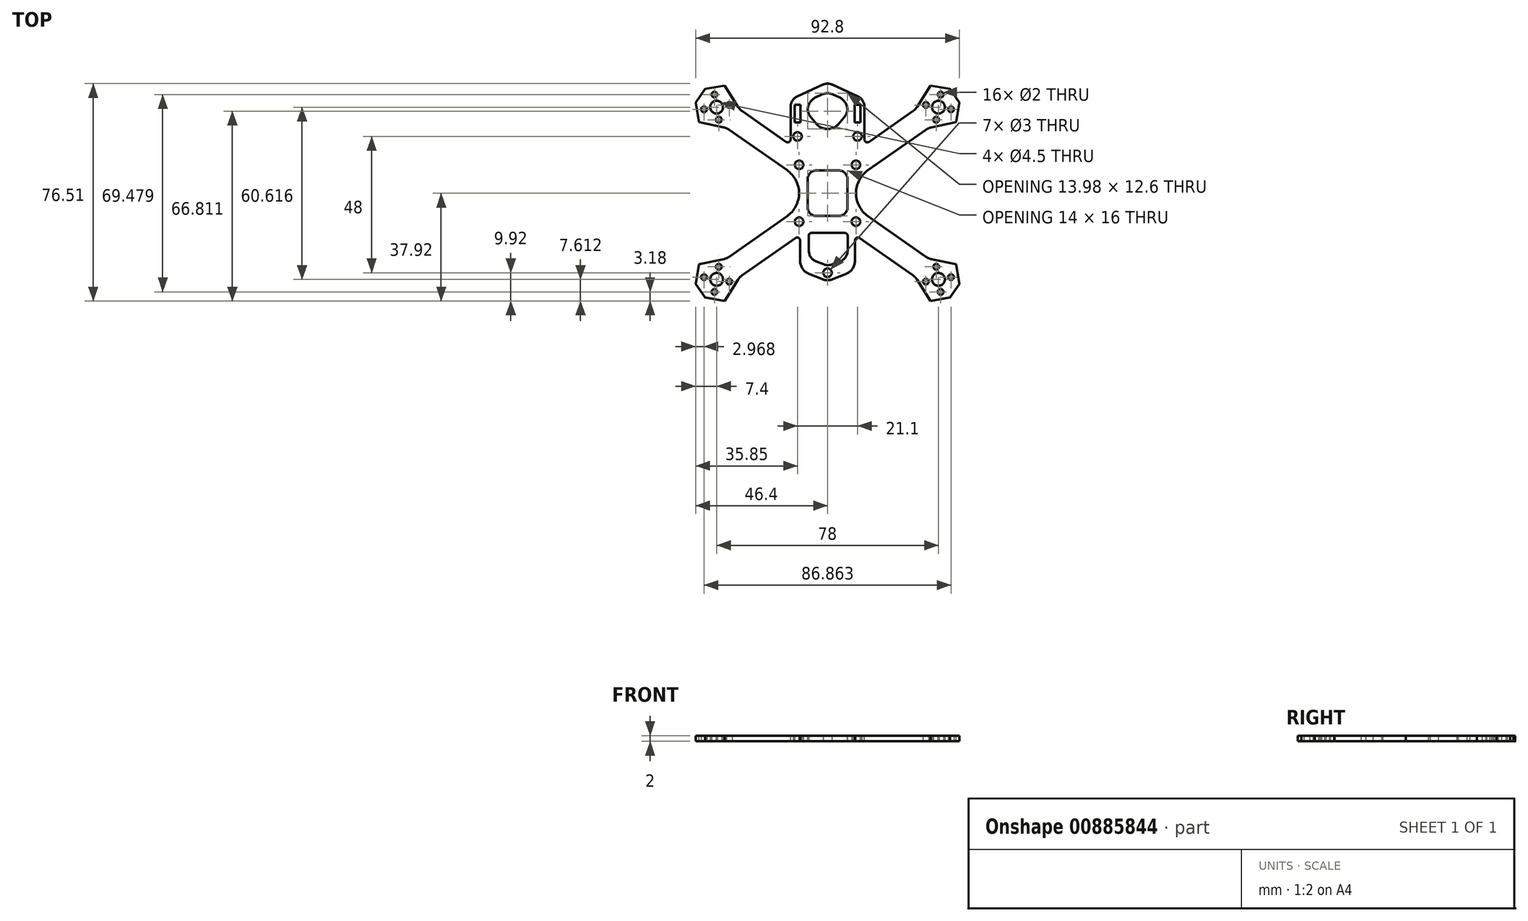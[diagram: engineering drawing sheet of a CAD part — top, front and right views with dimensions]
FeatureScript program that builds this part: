
annotation { "Feature Type Name" : "Feature", "Feature Type Description" : "" }
export const myFeature = defineFeature(function(context is Context, id is Id, definition is map)
    precondition{}
    {
        {
            var Q0;
            Q0=qCreatedBy(makeId("Top.planeOp"),FACE);
            var sketch = newSketch(context, id + "F0", { "sketchPlane" : qUnion([Q0])});
            skLineSegment(sketch, "E0.bottom", {"start": v(10, 10) * mm, "end": v(-10, 10) * mm, "construction": true});
            skLineSegment(sketch, "E0.top", {"start": v(10, -10) * mm, "end": v(-10, -10) * mm, "construction": true});
            skLineSegment(sketch, "E0.left", {"start": v(10, 10) * mm, "end": v(10, -10) * mm, "construction": true});
            skLineSegment(sketch, "E0.right", {"start": v(-10, 10) * mm, "end": v(-10, -10) * mm, "construction": true});
            skPoint(sketch, "E0.middle", {"position": v(0, 0) * mm});
            skCircle(sketch, "E1", {"center": v(-10, 10) * mm, "radius": 1.5 * mm});
            skCircle(sketch, "E2", {"center": v(10, 10) * mm, "radius": 1.5 * mm});
            skCircle(sketch, "E3", {"center": v(10, -10) * mm, "radius": 1.5 * mm});
            skCircle(sketch, "E4", {"center": v(-10, -10) * mm, "radius": 1.5 * mm});
            skLineSegment(sketch, "E5.bottom", {"start": v(13, 13) * mm, "end": v(-13, 13) * mm});
            skLineSegment(sketch, "E5.top", {"start": v(13, -13) * mm, "end": v(-13, -13) * mm});
            skLineSegment(sketch, "E5.left", {"start": v(13, 13) * mm, "end": v(13, -13) * mm});
            skLineSegment(sketch, "E5.right", {"start": v(-13, 13) * mm, "end": v(-13, -13) * mm});
            skLineSegment(sketch, "E6.bottom", {"start": v(-13, 13) * mm, "end": v(13, 13) * mm});
            skLineSegment(sketch, "E6.top", {"start": v(-13, 33) * mm, "end": v(13, 33) * mm});
            skLineSegment(sketch, "E6.left", {"start": v(-13, 13) * mm, "end": v(-13, 33) * mm});
            skLineSegment(sketch, "E6.right", {"start": v(13, 13) * mm, "end": v(13, 33) * mm});
            skLineSegment(sketch, "E7.bottom", {"start": v(-11.6, 24.9) * mm, "end": v(-9.5, 24.9) * mm});
            skLineSegment(sketch, "E7.top", {"start": v(-11.6, 31.1) * mm, "end": v(-9.5, 31.1) * mm});
            skLineSegment(sketch, "E7.left", {"start": v(-11.6, 24.9) * mm, "end": v(-11.6, 31.1) * mm});
            skLineSegment(sketch, "E7.right", {"start": v(-9.5, 24.9) * mm, "end": v(-9.5, 31.1) * mm});
            skLineSegment(sketch, "E8.bottom", {"start": v(9.5, 24.9) * mm, "end": v(11.6, 24.9) * mm});
            skLineSegment(sketch, "E8.top", {"start": v(9.5, 31.1) * mm, "end": v(11.6, 31.1) * mm});
            skLineSegment(sketch, "E8.left", {"start": v(9.5, 24.9) * mm, "end": v(9.5, 31.1) * mm});
            skLineSegment(sketch, "E8.right", {"start": v(11.6, 24.9) * mm, "end": v(11.6, 31.1) * mm});
            skLineSegment(sketch, "E9.bottom", {"start": v(-13, -13) * mm, "end": v(13, -13) * mm});
            skLineSegment(sketch, "E9.top", {"start": v(-13, -31) * mm, "end": v(13, -31) * mm});
            skLineSegment(sketch, "E9.left", {"start": v(-13, -13) * mm, "end": v(-13, -31) * mm});
            skLineSegment(sketch, "E9.right", {"start": v(13, -13) * mm, "end": v(13, -31) * mm});
            skCircle(sketch, "E10", {"center": v(-39, 30.3) * mm, "radius": 25.5 * mm, "construction": true});
            skCircle(sketch, "E11", {"center": v(39, 30.3) * mm, "radius": 25.5 * mm, "construction": true});
            skLineSegment(sketch, "E12", {"start": v(0, 0) * mm, "end": v(0, 3) * mm, "construction": true});
            skLineSegment(sketch, "E13", {"start": v(0, 3) * mm, "end": v(65.53, 48.89) * mm, "construction": true});
            skLineSegment(sketch, "E14", {"start": v(0, 3) * mm, "end": v(-65.53, 48.89) * mm, "construction": true});
            skCircle(sketch, "E15", {"center": v(-10.55, 20) * mm, "radius": 1.5 * mm});
            skPoint(sketch, "E15.centerSnap0", {"position": v(-10.55, 31.1) * mm});
            skCircle(sketch, "E16", {"center": v(10.55, 20) * mm, "radius": 1.5 * mm});
            skPoint(sketch, "E16.centerSnap0", {"position": v(10.55, 31.1) * mm});
            skLineSegment(sketch, "E17", {"start": v(34.98, 36.04) * mm, "end": v(43.02, 24.57) * mm, "construction": true});
            skArc(sketch, "E18", {"start": v(34.98, 36.04) * mm, "mid": v(44.73, 34.32) * mm, "end": v(43.02, 24.57) * mm});
            skLineSegment(sketch, "E19", {"start": v(34.98, 36.04) * mm, "end": v(13, 20.65) * mm});
            skLineSegment(sketch, "E20", {"start": v(43.02, 24.57) * mm, "end": v(13, 3.56) * mm});
            skLineSegment(sketch, "E21", {"start": v(-34.98, 36.04) * mm, "end": v(-43.02, 24.57) * mm, "construction": true});
            skArc(sketch, "E22", {"start": v(-43.02, 24.57) * mm, "mid": v(-44.73, 34.32) * mm, "end": v(-34.98, 36.04) * mm});
            skLineSegment(sketch, "E23", {"start": v(-34.98, 36.04) * mm, "end": v(-13, 20.65) * mm});
            skLineSegment(sketch, "E24", {"start": v(-43.02, 24.57) * mm, "end": v(-13, 3.56) * mm});
            skCircle(sketch, "E25", {"center": v(-39, 30.3) * mm, "radius": 4.5 * mm, "construction": true});
            skCircle(sketch, "E26", {"center": v(-43.43, 29.53) * mm, "radius": 1 * mm});
            skCircle(sketch, "E27", {"center": v(-34.57, 31.09) * mm, "radius": 1 * mm});
            skCircle(sketch, "E28", {"center": v(-39.78, 34.74) * mm, "radius": 1 * mm});
            skCircle(sketch, "E29", {"center": v(-38.22, 25.88) * mm, "radius": 1 * mm});
            skCircle(sketch, "E30", {"center": v(-39, 30.3) * mm, "radius": 2.25 * mm});
            skLineSegment(sketch, "E31", {"start": v(0, 0) * mm, "end": v(0, -3) * mm, "construction": true});
            skLineSegment(sketch, "E32", {"start": v(0, -3) * mm, "end": v(65.53, -48.89) * mm, "construction": true});
            skLineSegment(sketch, "E33", {"start": v(0, -3) * mm, "end": v(-65.53, -48.89) * mm, "construction": true});
            skLineSegment(sketch, "E34", {"start": v(34.98, -36.04) * mm, "end": v(43.02, -24.57) * mm, "construction": true});
            skCircle(sketch, "E35", {"center": v(39, -30.3) * mm, "radius": 25.5 * mm, "construction": true});
            skArc(sketch, "E36", {"start": v(43.02, -24.57) * mm, "mid": v(44.73, -34.32) * mm, "end": v(34.98, -36.04) * mm});
            skLineSegment(sketch, "E37", {"start": v(34.98, -36.04) * mm, "end": v(13, -20.65) * mm});
            skLineSegment(sketch, "E38", {"start": v(43.02, -24.57) * mm, "end": v(13, -3.56) * mm});
            skLineSegment(sketch, "E39", {"start": v(-43.02, -24.57) * mm, "end": v(-34.98, -36.04) * mm, "construction": true});
            skArc(sketch, "E40", {"start": v(-34.98, -36.04) * mm, "mid": v(-44.73, -34.32) * mm, "end": v(-43.02, -24.57) * mm});
            skLineSegment(sketch, "E41", {"start": v(-43.02, -24.57) * mm, "end": v(-13, -3.56) * mm});
            skLineSegment(sketch, "E42", {"start": v(-34.98, -36.04) * mm, "end": v(-13, -20.65) * mm});
            skCircle(sketch, "E43", {"center": v(39, 30.3) * mm, "radius": 4.5 * mm, "construction": true});
            skCircle(sketch, "E44", {"center": v(43.43, 29.53) * mm, "radius": 1 * mm});
            skCircle(sketch, "E45", {"center": v(34.57, 31.09) * mm, "radius": 1 * mm});
            skCircle(sketch, "E46", {"center": v(39.78, 34.74) * mm, "radius": 1 * mm});
            skCircle(sketch, "E47", {"center": v(38.22, 25.88) * mm, "radius": 1 * mm});
            skCircle(sketch, "E48", {"center": v(39, 30.3) * mm, "radius": 2.25 * mm});
            skCircle(sketch, "E49", {"center": v(-39, -30.3) * mm, "radius": 4.5 * mm, "construction": true});
            skCircle(sketch, "E50", {"center": v(-43.43, -29.53) * mm, "radius": 1 * mm});
            skCircle(sketch, "E51", {"center": v(-34.57, -31.09) * mm, "radius": 1 * mm});
            skCircle(sketch, "E52", {"center": v(-38.22, -25.88) * mm, "radius": 1 * mm});
            skCircle(sketch, "E53", {"center": v(-39.78, -34.74) * mm, "radius": 1 * mm});
            skCircle(sketch, "E54", {"center": v(-39, -30.3) * mm, "radius": 2.25 * mm});
            skCircle(sketch, "E55", {"center": v(39, -30.3) * mm, "radius": 4.5 * mm, "construction": true});
            skCircle(sketch, "E56", {"center": v(43.43, -29.53) * mm, "radius": 1 * mm});
            skCircle(sketch, "E57", {"center": v(38.22, -25.88) * mm, "radius": 1 * mm});
            skCircle(sketch, "E58", {"center": v(34.57, -31.09) * mm, "radius": 1 * mm});
            skCircle(sketch, "E59", {"center": v(39.78, -34.74) * mm, "radius": 1 * mm});
            skCircle(sketch, "E60", {"center": v(39, -30.3) * mm, "radius": 2.25 * mm});
            skCircle(sketch, "E61", {"center": v(-39, -30.3) * mm, "radius": 25.5 * mm, "construction": true});
            skCircle(sketch, "E62", {"center": v(0, -28) * mm, "radius": 1.5 * mm});
            skPoint(sketch, "E62.centerSnap0", {"position": v(0, -31) * mm});
            skLineSegment(sketch, "E63", {"start": v(-45.9, 29.1) * mm, "end": v(-32.1, 31.52) * mm, "construction": true});
            skLineSegment(sketch, "E64", {"start": v(-40.22, 37.2) * mm, "end": v(-37.78, 23.41) * mm, "construction": true});
            skLineSegment(sketch, "E65", {"start": v(40.22, 37.2) * mm, "end": v(37.78, 23.41) * mm, "construction": true});
            skLineSegment(sketch, "E66", {"start": v(45.9, 29.1) * mm, "end": v(32.1, 31.52) * mm, "construction": true});
            skLineSegment(sketch, "E67", {"start": v(-45.9, -29.1) * mm, "end": v(-32.1, -31.52) * mm, "construction": true});
            skLineSegment(sketch, "E68", {"start": v(-40.22, -37.2) * mm, "end": v(-37.78, -23.41) * mm, "construction": true});
            skLineSegment(sketch, "E69", {"start": v(45.9, -29.1) * mm, "end": v(32.1, -31.52) * mm, "construction": true});
            skLineSegment(sketch, "E70", {"start": v(40.22, -37.2) * mm, "end": v(37.78, -23.41) * mm, "construction": true});
            skSolve(sketch);
        }
        {
            var Q0;
            Q0 = qSketchRegion(id + "F0", true);
            extrude(context, id + "F1", {"entities" : qUnion([Q0]), "depth" : 2 * mm, "offsetDistance" : 25 * mm});
        }
        {
            var Q0;
            Q0=makeQuery(id+"F1.opExtrude","CAP_FACE",FACE,{"disambiguationData":[OSD([sQuery(id+"F0.wireOp",EDGE,"E1"),sQuery(id+"F0.wireOp",EDGE,"E2"),sQuery(id+"F0.wireOp",EDGE,"E3"),sQuery(id+"F0.wireOp",EDGE,"E4"),sQuery(id+"F0.wireOp",EDGE,"E5.left"),sQuery(id+"F0.wireOp",EDGE,"E5.right"),sQuery(id+"F0.wireOp",EDGE,"E6.top"),sQuery(id+"F0.wireOp",EDGE,"E6.left"),sQuery(id+"F0.wireOp",EDGE,"E6.right"),sQuery(id+"F0.wireOp",EDGE,"E7.bottom"),sQuery(id+"F0.wireOp",EDGE,"E7.top"),sQuery(id+"F0.wireOp",EDGE,"E7.left"),sQuery(id+"F0.wireOp",EDGE,"E7.right"),sQuery(id+"F0.wireOp",EDGE,"E8.bottom"),sQuery(id+"F0.wireOp",EDGE,"E8.top"),sQuery(id+"F0.wireOp",EDGE,"E8.left"),sQuery(id+"F0.wireOp",EDGE,"E8.right"),sQuery(id+"F0.wireOp",EDGE,"E9.top"),sQuery(id+"F0.wireOp",EDGE,"E9.left"),sQuery(id+"F0.wireOp",EDGE,"E9.right"),sQuery(id+"F0.wireOp",EDGE,"E15"),sQuery(id+"F0.wireOp",EDGE,"E16"),sQuery(id+"F0.wireOp",EDGE,"E18"),sQuery(id+"F0.wireOp",EDGE,"E19"),sQuery(id+"F0.wireOp",EDGE,"E20"),sQuery(id+"F0.wireOp",EDGE,"E22"),sQuery(id+"F0.wireOp",EDGE,"E23"),sQuery(id+"F0.wireOp",EDGE,"E24"),sQuery(id+"F0.wireOp",EDGE,"E26"),sQuery(id+"F0.wireOp",EDGE,"E27"),sQuery(id+"F0.wireOp",EDGE,"E28"),sQuery(id+"F0.wireOp",EDGE,"E29"),sQuery(id+"F0.wireOp",EDGE,"E30"),sQuery(id+"F0.wireOp",EDGE,"E36"),sQuery(id+"F0.wireOp",EDGE,"E37"),sQuery(id+"F0.wireOp",EDGE,"E38"),sQuery(id+"F0.wireOp",EDGE,"E40"),sQuery(id+"F0.wireOp",EDGE,"E41"),sQuery(id+"F0.wireOp",EDGE,"E42"),sQuery(id+"F0.wireOp",EDGE,"E44"),sQuery(id+"F0.wireOp",EDGE,"E45"),sQuery(id+"F0.wireOp",EDGE,"E46"),sQuery(id+"F0.wireOp",EDGE,"E47"),sQuery(id+"F0.wireOp",EDGE,"E48"),sQuery(id+"F0.wireOp",EDGE,"E50"),sQuery(id+"F0.wireOp",EDGE,"E51"),sQuery(id+"F0.wireOp",EDGE,"E52"),sQuery(id+"F0.wireOp",EDGE,"E53"),sQuery(id+"F0.wireOp",EDGE,"E54"),sQuery(id+"F0.wireOp",EDGE,"E56"),sQuery(id+"F0.wireOp",EDGE,"E57"),sQuery(id+"F0.wireOp",EDGE,"E58"),sQuery(id+"F0.wireOp",EDGE,"E59"),sQuery(id+"F0.wireOp",EDGE,"E60")])],"isStart":false});
            var sketch = newSketch(context, id + "F2", { "sketchPlane" : qUnion([Q0])});
            skLineSegment(sketch, "E71", {"start": v(-13, 33) * mm, "end": v(0, 39) * mm});
            skLineSegment(sketch, "E72", {"start": v(0, 39) * mm, "end": v(13, 33) * mm});
            skLineSegment(sketch, "E73", {"start": v(-13, 33) * mm, "end": v(-13, 32) * mm});
            skLineSegment(sketch, "E74", {"start": v(-13, 32) * mm, "end": v(13, 32) * mm});
            skLineSegment(sketch, "E75", {"start": v(13, 32) * mm, "end": v(13, 33) * mm});
            skSolve(sketch);
        }
        {
            var Q0;
            Q0 = qSketchRegion(id + "F2", true);
            var Q1;
            Q1=makeQuery(id+"F1.opExtrude","CAP_FACE",FACE,{"disambiguationData":[OSD([sQuery(id+"F0.wireOp",EDGE,"E1"),sQuery(id+"F0.wireOp",EDGE,"E2"),sQuery(id+"F0.wireOp",EDGE,"E3"),sQuery(id+"F0.wireOp",EDGE,"E4"),sQuery(id+"F0.wireOp",EDGE,"E5.left"),sQuery(id+"F0.wireOp",EDGE,"E5.right"),sQuery(id+"F0.wireOp",EDGE,"E6.top"),sQuery(id+"F0.wireOp",EDGE,"E6.left"),sQuery(id+"F0.wireOp",EDGE,"E6.right"),sQuery(id+"F0.wireOp",EDGE,"E7.bottom"),sQuery(id+"F0.wireOp",EDGE,"E7.top"),sQuery(id+"F0.wireOp",EDGE,"E7.left"),sQuery(id+"F0.wireOp",EDGE,"E7.right"),sQuery(id+"F0.wireOp",EDGE,"E8.bottom"),sQuery(id+"F0.wireOp",EDGE,"E8.top"),sQuery(id+"F0.wireOp",EDGE,"E8.left"),sQuery(id+"F0.wireOp",EDGE,"E8.right"),sQuery(id+"F0.wireOp",EDGE,"E9.top"),sQuery(id+"F0.wireOp",EDGE,"E9.left"),sQuery(id+"F0.wireOp",EDGE,"E9.right"),sQuery(id+"F0.wireOp",EDGE,"E15"),sQuery(id+"F0.wireOp",EDGE,"E16"),sQuery(id+"F0.wireOp",EDGE,"E18"),sQuery(id+"F0.wireOp",EDGE,"E19"),sQuery(id+"F0.wireOp",EDGE,"E20"),sQuery(id+"F0.wireOp",EDGE,"E22"),sQuery(id+"F0.wireOp",EDGE,"E23"),sQuery(id+"F0.wireOp",EDGE,"E24"),sQuery(id+"F0.wireOp",EDGE,"E26"),sQuery(id+"F0.wireOp",EDGE,"E27"),sQuery(id+"F0.wireOp",EDGE,"E28"),sQuery(id+"F0.wireOp",EDGE,"E29"),sQuery(id+"F0.wireOp",EDGE,"E30"),sQuery(id+"F0.wireOp",EDGE,"E36"),sQuery(id+"F0.wireOp",EDGE,"E37"),sQuery(id+"F0.wireOp",EDGE,"E38"),sQuery(id+"F0.wireOp",EDGE,"E40"),sQuery(id+"F0.wireOp",EDGE,"E41"),sQuery(id+"F0.wireOp",EDGE,"E42"),sQuery(id+"F0.wireOp",EDGE,"E44"),sQuery(id+"F0.wireOp",EDGE,"E45"),sQuery(id+"F0.wireOp",EDGE,"E46"),sQuery(id+"F0.wireOp",EDGE,"E47"),sQuery(id+"F0.wireOp",EDGE,"E48"),sQuery(id+"F0.wireOp",EDGE,"E50"),sQuery(id+"F0.wireOp",EDGE,"E51"),sQuery(id+"F0.wireOp",EDGE,"E52"),sQuery(id+"F0.wireOp",EDGE,"E53"),sQuery(id+"F0.wireOp",EDGE,"E54"),sQuery(id+"F0.wireOp",EDGE,"E56"),sQuery(id+"F0.wireOp",EDGE,"E57"),sQuery(id+"F0.wireOp",EDGE,"E58"),sQuery(id+"F0.wireOp",EDGE,"E59"),sQuery(id+"F0.wireOp",EDGE,"E60")])],"isStart":true});
            extrude(context, id + "F3", {"entities" : qUnion([Q0]), "operationType" : NewBodyOperationType.ADD, "endBound" : BoundingType.UP_TO_SURFACE, "oppositeDirection" : true, "depth" : 25 * mm, "endBoundEntityFace" : qUnion([Q1]), "offsetDistance" : 25 * mm});
        }
        {
            var Q0;
            {var subQ0=sQuery(id+"F0.wireOp",EDGE,"E6.top");Q0=makeQuery(id+"F3.boolean.opBoolean","MERGE",EDGE,{"derivedFrom":[makeQuery(id+"F1.opExtrude","SWEPT_EDGE",EDGE,{"disambiguationData":[OSD([subQ0,sQuery(id+"F0.wireOp",EDGE,"E6.left")])]}),makeQuery(id+"F3.opExtrude","SWEPT_EDGE",EDGE,{"disambiguationData":[OSD([subQ0,sQuery(id+"F2.wireOp",EDGE,"E71"),sQuery(id+"F2.wireOp",EDGE,"E73")])]})]});}
            var Q1;
            Q1=makeQuery(id+"F3.opExtrude","SWEPT_EDGE",EDGE,{"disambiguationData":[OSD([sQuery(id+"F2.wireOp",EDGE,"E71"),sQuery(id+"F2.wireOp",EDGE,"E72")])]});
            var Q2;
            {var subQ0=sQuery(id+"F0.wireOp",EDGE,"E6.top");Q2=makeQuery(id+"F3.boolean.opBoolean","MERGE",EDGE,{"derivedFrom":[makeQuery(id+"F1.opExtrude","SWEPT_EDGE",EDGE,{"disambiguationData":[OSD([subQ0,sQuery(id+"F0.wireOp",EDGE,"E6.right")])]}),makeQuery(id+"F3.opExtrude","SWEPT_EDGE",EDGE,{"disambiguationData":[OSD([subQ0,sQuery(id+"F2.wireOp",EDGE,"E72"),sQuery(id+"F2.wireOp",EDGE,"E75")])]})]});}
            fillet(context, id + "F4", {"entities" : qUnion([Q0, Q1, Q2]), "radius" : 4 * mm, "tangentPropagation" : true, "allowEdgeOverflow" : false});
        }
        {
            var Q0;
            Q0=makeQuery(id+"F3.boolean.opBoolean","MERGE",FACE,{"derivedFrom":[makeQuery(id+"F1.opExtrude","CAP_FACE",FACE,{"disambiguationData":[OSD([sQuery(id+"F0.wireOp",EDGE,"E1"),sQuery(id+"F0.wireOp",EDGE,"E2"),sQuery(id+"F0.wireOp",EDGE,"E3"),sQuery(id+"F0.wireOp",EDGE,"E4"),sQuery(id+"F0.wireOp",EDGE,"E5.left"),sQuery(id+"F0.wireOp",EDGE,"E5.right"),sQuery(id+"F0.wireOp",EDGE,"E6.top"),sQuery(id+"F0.wireOp",EDGE,"E6.left"),sQuery(id+"F0.wireOp",EDGE,"E6.right"),sQuery(id+"F0.wireOp",EDGE,"E7.bottom"),sQuery(id+"F0.wireOp",EDGE,"E7.top"),sQuery(id+"F0.wireOp",EDGE,"E7.left"),sQuery(id+"F0.wireOp",EDGE,"E7.right"),sQuery(id+"F0.wireOp",EDGE,"E8.bottom"),sQuery(id+"F0.wireOp",EDGE,"E8.top"),sQuery(id+"F0.wireOp",EDGE,"E8.left"),sQuery(id+"F0.wireOp",EDGE,"E8.right"),sQuery(id+"F0.wireOp",EDGE,"E9.top"),sQuery(id+"F0.wireOp",EDGE,"E9.left"),sQuery(id+"F0.wireOp",EDGE,"E9.right"),sQuery(id+"F0.wireOp",EDGE,"E15"),sQuery(id+"F0.wireOp",EDGE,"E16"),sQuery(id+"F0.wireOp",EDGE,"E18"),sQuery(id+"F0.wireOp",EDGE,"E19"),sQuery(id+"F0.wireOp",EDGE,"E20"),sQuery(id+"F0.wireOp",EDGE,"E22"),sQuery(id+"F0.wireOp",EDGE,"E23"),sQuery(id+"F0.wireOp",EDGE,"E24"),sQuery(id+"F0.wireOp",EDGE,"E26"),sQuery(id+"F0.wireOp",EDGE,"E27"),sQuery(id+"F0.wireOp",EDGE,"E28"),sQuery(id+"F0.wireOp",EDGE,"E29"),sQuery(id+"F0.wireOp",EDGE,"E30"),sQuery(id+"F0.wireOp",EDGE,"E36"),sQuery(id+"F0.wireOp",EDGE,"E37"),sQuery(id+"F0.wireOp",EDGE,"E38"),sQuery(id+"F0.wireOp",EDGE,"E40"),sQuery(id+"F0.wireOp",EDGE,"E41"),sQuery(id+"F0.wireOp",EDGE,"E42"),sQuery(id+"F0.wireOp",EDGE,"E44"),sQuery(id+"F0.wireOp",EDGE,"E45"),sQuery(id+"F0.wireOp",EDGE,"E46"),sQuery(id+"F0.wireOp",EDGE,"E47"),sQuery(id+"F0.wireOp",EDGE,"E48"),sQuery(id+"F0.wireOp",EDGE,"E50"),sQuery(id+"F0.wireOp",EDGE,"E51"),sQuery(id+"F0.wireOp",EDGE,"E52"),sQuery(id+"F0.wireOp",EDGE,"E53"),sQuery(id+"F0.wireOp",EDGE,"E54"),sQuery(id+"F0.wireOp",EDGE,"E56"),sQuery(id+"F0.wireOp",EDGE,"E57"),sQuery(id+"F0.wireOp",EDGE,"E58"),sQuery(id+"F0.wireOp",EDGE,"E59"),sQuery(id+"F0.wireOp",EDGE,"E60")])],"isStart":false}),makeQuery(id+"F3.opExtrude","CAP_FACE",FACE,{"disambiguationData":[OSD([sQuery(id+"F2.wireOp",EDGE,"E71"),sQuery(id+"F2.wireOp",EDGE,"E72"),sQuery(id+"F2.wireOp",EDGE,"E73"),sQuery(id+"F2.wireOp",EDGE,"E74"),sQuery(id+"F2.wireOp",EDGE,"E75")])],"isStart":true})]});
            var sketch = newSketch(context, id + "F5", { "sketchPlane" : qUnion([Q0])});
            skLineSegment(sketch, "E76", {"start": v(0, 35.7) * mm, "end": v(-7, 32.47) * mm});
            skLineSegment(sketch, "E77", {"start": v(-7, 32.47) * mm, "end": v(-7, 28) * mm});
            skPoint(sketch, "E77.endSnap0", {"position": v(-9.5, 28) * mm});
            skLineSegment(sketch, "E78", {"start": v(-7, 28) * mm, "end": v(0, 20) * mm});
            skLineSegment(sketch, "E79", {"start": v(0, 20) * mm, "end": v(7, 28) * mm});
            skLineSegment(sketch, "E80", {"start": v(7, 28) * mm, "end": v(7, 32.47) * mm});
            skLineSegment(sketch, "E81", {"start": v(7, 32.47) * mm, "end": v(0, 35.7) * mm});
            skSolve(sketch);
        }
        {
            var Q0;
            Q0 = qSketchRegion(id + "F5", true);
            extrude(context, id + "F6", {"entities" : qUnion([Q0]), "operationType" : NewBodyOperationType.REMOVE, "endBound" : BoundingType.THROUGH_ALL, "oppositeDirection" : true, "depth" : 25 * mm, "offsetDistance" : 25 * mm});
        }
        {
            var Q0;
            Q0=makeQuery(id+"F6.boolean.opBoolean","COPY",EDGE,{"derivedFrom":makeQuery(id+"F6.opExtrude","SWEPT_EDGE",EDGE,{"disambiguationData":[OSD([sQuery(id+"F5.wireOp",EDGE,"E76"),sQuery(id+"F5.wireOp",EDGE,"E81")])]})});
            var Q1;
            Q1=makeQuery(id+"F6.boolean.opBoolean","COPY",EDGE,{"derivedFrom":makeQuery(id+"F6.opExtrude","SWEPT_EDGE",EDGE,{"disambiguationData":[OSD([sQuery(id+"F5.wireOp",EDGE,"E76"),sQuery(id+"F5.wireOp",EDGE,"E77")])]})});
            var Q2;
            Q2=makeQuery(id+"F6.boolean.opBoolean","COPY",EDGE,{"derivedFrom":makeQuery(id+"F6.opExtrude","SWEPT_EDGE",EDGE,{"disambiguationData":[OSD([sQuery(id+"F5.wireOp",EDGE,"E80"),sQuery(id+"F5.wireOp",EDGE,"E81")])]})});
            var Q3;
            Q3=makeQuery(id+"F6.boolean.opBoolean","COPY",EDGE,{"derivedFrom":makeQuery(id+"F6.opExtrude","SWEPT_EDGE",EDGE,{"disambiguationData":[OSD([sQuery(id+"F5.wireOp",EDGE,"E79"),sQuery(id+"F5.wireOp",EDGE,"E80")])]})});
            var Q4;
            Q4=makeQuery(id+"F6.boolean.opBoolean","COPY",EDGE,{"derivedFrom":makeQuery(id+"F6.opExtrude","SWEPT_EDGE",EDGE,{"disambiguationData":[OSD([sQuery(id+"F5.wireOp",EDGE,"E77"),sQuery(id+"F5.wireOp",EDGE,"E78")])]})});
            var Q5;
            Q5=makeQuery(id+"F6.boolean.opBoolean","COPY",EDGE,{"derivedFrom":makeQuery(id+"F6.opExtrude","SWEPT_EDGE",EDGE,{"disambiguationData":[OSD([sQuery(id+"F5.wireOp",EDGE,"E78"),sQuery(id+"F5.wireOp",EDGE,"E79")])]})});
            fillet(context, id + "F7", {"entities" : qUnion([Q0, Q1, Q2, Q3, Q4, Q5]), "radius" : 5 * mm, "tangentPropagation" : true, "allowEdgeOverflow" : false});
        }
        {
            var Q0;
            Q0=makeQuery(id+"F3.boolean.opBoolean","MERGE",FACE,{"derivedFrom":[makeQuery(id+"F1.opExtrude","CAP_FACE",FACE,{"disambiguationData":[OSD([sQuery(id+"F0.wireOp",EDGE,"E1"),sQuery(id+"F0.wireOp",EDGE,"E2"),sQuery(id+"F0.wireOp",EDGE,"E3"),sQuery(id+"F0.wireOp",EDGE,"E4"),sQuery(id+"F0.wireOp",EDGE,"E5.left"),sQuery(id+"F0.wireOp",EDGE,"E5.right"),sQuery(id+"F0.wireOp",EDGE,"E6.top"),sQuery(id+"F0.wireOp",EDGE,"E6.left"),sQuery(id+"F0.wireOp",EDGE,"E6.right"),sQuery(id+"F0.wireOp",EDGE,"E7.bottom"),sQuery(id+"F0.wireOp",EDGE,"E7.top"),sQuery(id+"F0.wireOp",EDGE,"E7.left"),sQuery(id+"F0.wireOp",EDGE,"E7.right"),sQuery(id+"F0.wireOp",EDGE,"E8.bottom"),sQuery(id+"F0.wireOp",EDGE,"E8.top"),sQuery(id+"F0.wireOp",EDGE,"E8.left"),sQuery(id+"F0.wireOp",EDGE,"E8.right"),sQuery(id+"F0.wireOp",EDGE,"E9.top"),sQuery(id+"F0.wireOp",EDGE,"E9.left"),sQuery(id+"F0.wireOp",EDGE,"E9.right"),sQuery(id+"F0.wireOp",EDGE,"E15"),sQuery(id+"F0.wireOp",EDGE,"E16"),sQuery(id+"F0.wireOp",EDGE,"E18"),sQuery(id+"F0.wireOp",EDGE,"E19"),sQuery(id+"F0.wireOp",EDGE,"E20"),sQuery(id+"F0.wireOp",EDGE,"E22"),sQuery(id+"F0.wireOp",EDGE,"E23"),sQuery(id+"F0.wireOp",EDGE,"E24"),sQuery(id+"F0.wireOp",EDGE,"E26"),sQuery(id+"F0.wireOp",EDGE,"E27"),sQuery(id+"F0.wireOp",EDGE,"E28"),sQuery(id+"F0.wireOp",EDGE,"E29"),sQuery(id+"F0.wireOp",EDGE,"E30"),sQuery(id+"F0.wireOp",EDGE,"E36"),sQuery(id+"F0.wireOp",EDGE,"E37"),sQuery(id+"F0.wireOp",EDGE,"E38"),sQuery(id+"F0.wireOp",EDGE,"E40"),sQuery(id+"F0.wireOp",EDGE,"E41"),sQuery(id+"F0.wireOp",EDGE,"E42"),sQuery(id+"F0.wireOp",EDGE,"E44"),sQuery(id+"F0.wireOp",EDGE,"E45"),sQuery(id+"F0.wireOp",EDGE,"E46"),sQuery(id+"F0.wireOp",EDGE,"E47"),sQuery(id+"F0.wireOp",EDGE,"E48"),sQuery(id+"F0.wireOp",EDGE,"E50"),sQuery(id+"F0.wireOp",EDGE,"E51"),sQuery(id+"F0.wireOp",EDGE,"E52"),sQuery(id+"F0.wireOp",EDGE,"E53"),sQuery(id+"F0.wireOp",EDGE,"E54"),sQuery(id+"F0.wireOp",EDGE,"E56"),sQuery(id+"F0.wireOp",EDGE,"E57"),sQuery(id+"F0.wireOp",EDGE,"E58"),sQuery(id+"F0.wireOp",EDGE,"E59"),sQuery(id+"F0.wireOp",EDGE,"E60")])],"isStart":false}),makeQuery(id+"F3.opExtrude","CAP_FACE",FACE,{"disambiguationData":[OSD([sQuery(id+"F2.wireOp",EDGE,"E71"),sQuery(id+"F2.wireOp",EDGE,"E72"),sQuery(id+"F2.wireOp",EDGE,"E73"),sQuery(id+"F2.wireOp",EDGE,"E74"),sQuery(id+"F2.wireOp",EDGE,"E75")])],"isStart":true})]});
            var sketch = newSketch(context, id + "F8", { "sketchPlane" : qUnion([Q0])});
            skLineSegment(sketch, "E82", {"start": v(-30.92, 29.53) * mm, "end": v(-13, 16.99) * mm});
            skLineSegment(sketch, "E83", {"start": v(-10, 5.12) * mm, "end": v(-35.5, 22.98) * mm});
            skLineSegment(sketch, "E84", {"start": v(-13, 16.99) * mm, "end": v(-13, 25.54) * mm});
            skLineSegment(sketch, "E85", {"start": v(-13, 25.54) * mm, "end": v(-34.98, 40.94) * mm});
            skLineSegment(sketch, "E86", {"start": v(-13, 0) * mm, "end": v(-43.02, 21.02) * mm});
            skLineSegment(sketch, "E87", {"start": v(-43.02, 21.02) * mm, "end": v(-43.02, 24.57) * mm});
            skLineSegment(sketch, "E88", {"start": v(-34.98, 36.04) * mm, "end": v(-34.98, 40.94) * mm});
            skLineSegment(sketch, "E89", {"start": v(13, 16.99) * mm, "end": v(30.92, 29.53) * mm});
            skLineSegment(sketch, "E90", {"start": v(10, 5.12) * mm, "end": v(35.5, 22.98) * mm});
            skLineSegment(sketch, "E91", {"start": v(13, 16.99) * mm, "end": v(13, 25.54) * mm});
            skLineSegment(sketch, "E92", {"start": v(13, 25.54) * mm, "end": v(34.98, 40.94) * mm});
            skLineSegment(sketch, "E93", {"start": v(34.98, 40.94) * mm, "end": v(34.98, 36.04) * mm});
            skLineSegment(sketch, "E94", {"start": v(13, 0) * mm, "end": v(43.02, 21.02) * mm});
            skLineSegment(sketch, "E95", {"start": v(43.02, 21.02) * mm, "end": v(43.02, 24.57) * mm});
            skLineSegment(sketch, "E96", {"start": v(13, -25.82) * mm, "end": v(34.98, -41.22) * mm});
            skLineSegment(sketch, "E97", {"start": v(34.98, -41.22) * mm, "end": v(34.98, -36.04) * mm});
            skLineSegment(sketch, "E98", {"start": v(13, -25.82) * mm, "end": v(13, -16.99) * mm});
            skLineSegment(sketch, "E99", {"start": v(13, -16.99) * mm, "end": v(30.92, -29.53) * mm});
            skLineSegment(sketch, "E100", {"start": v(35.5, -22.98) * mm, "end": v(10, -5.12) * mm});
            skLineSegment(sketch, "E101", {"start": v(13, 0) * mm, "end": v(43.02, -21.02) * mm});
            skLineSegment(sketch, "E102", {"start": v(43.02, -21.02) * mm, "end": v(43.02, -24.57) * mm});
            skLineSegment(sketch, "E103", {"start": v(-35.5, -22.98) * mm, "end": v(-10, -5.12) * mm});
            skLineSegment(sketch, "E104", {"start": v(-13, 0) * mm, "end": v(-43.02, -21.02) * mm});
            skLineSegment(sketch, "E105", {"start": v(-43.02, -21.02) * mm, "end": v(-43.02, -24.57) * mm});
            skLineSegment(sketch, "E106", {"start": v(-30.92, -29.53) * mm, "end": v(-13, -16.99) * mm});
            skLineSegment(sketch, "E107", {"start": v(-13, -16.99) * mm, "end": v(-13, -25.82) * mm});
            skLineSegment(sketch, "E108", {"start": v(-13, -25.82) * mm, "end": v(-34.98, -41.22) * mm});
            skLineSegment(sketch, "E109", {"start": v(-34.98, -41.22) * mm, "end": v(-34.98, -36.04) * mm});
            skLineSegment(sketch, "E110", {"start": v(-43.02, 24.57) * mm, "end": v(-35.5, 22.98) * mm});
            skLineSegment(sketch, "E111", {"start": v(-34.98, 36.04) * mm, "end": v(-30.92, 29.53) * mm});
            skLineSegment(sketch, "E112", {"start": v(30.92, 29.53) * mm, "end": v(34.98, 36.04) * mm});
            skLineSegment(sketch, "E113", {"start": v(35.5, 22.98) * mm, "end": v(43.02, 24.57) * mm});
            skLineSegment(sketch, "E114", {"start": v(-43.02, -24.57) * mm, "end": v(-35.5, -22.98) * mm});
            skLineSegment(sketch, "E115", {"start": v(-30.92, -29.53) * mm, "end": v(-34.98, -36.04) * mm});
            skLineSegment(sketch, "E116", {"start": v(35.5, -22.98) * mm, "end": v(43.02, -24.57) * mm});
            skLineSegment(sketch, "E117", {"start": v(30.92, -29.53) * mm, "end": v(34.98, -36.04) * mm});
            skLineSegment(sketch, "E118", {"start": v(-10, 5.12) * mm, "end": v(-10, -5.12) * mm});
            skLineSegment(sketch, "E119", {"start": v(10, 5.12) * mm, "end": v(10, -5.12) * mm});
            skSolve(sketch);
        }
        {
            var Q0;
            Q0 = qSketchRegion(id + "F8", true);
            extrude(context, id + "F9", {"entities" : qUnion([Q0]), "operationType" : NewBodyOperationType.REMOVE, "endBound" : BoundingType.THROUGH_ALL, "oppositeDirection" : true, "depth" : 25 * mm, "offsetDistance" : 25 * mm});
        }
        {
            var Q0;
            Q0=makeQuery(id+"F9.boolean.opBoolean","COPY",EDGE,{"derivedFrom":makeQuery(id+"F9.opExtrude","SWEPT_EDGE",EDGE,{"disambiguationData":[OSD([sQuery(id+"F8.wireOp",EDGE,"E99"),sQuery(id+"F8.wireOp",EDGE,"E117")])]})});
            var Q1;
            Q1=makeQuery(id+"F9.boolean.opBoolean","COPY",EDGE,{"derivedFrom":makeQuery(id+"F9.opExtrude","SWEPT_EDGE",EDGE,{"disambiguationData":[OSD([sQuery(id+"F8.wireOp",EDGE,"E89"),sQuery(id+"F8.wireOp",EDGE,"E112")])]})});
            var Q2;
            Q2=makeQuery(id+"F9.boolean.opBoolean","COPY",EDGE,{"derivedFrom":makeQuery(id+"F9.opExtrude","SWEPT_EDGE",EDGE,{"disambiguationData":[OSD([sQuery(id+"F8.wireOp",EDGE,"E82"),sQuery(id+"F8.wireOp",EDGE,"E111")])]})});
            var Q3;
            Q3=makeQuery(id+"F9.boolean.opBoolean","COPY",EDGE,{"derivedFrom":makeQuery(id+"F9.opExtrude","SWEPT_EDGE",EDGE,{"disambiguationData":[OSD([sQuery(id+"F8.wireOp",EDGE,"E83"),sQuery(id+"F8.wireOp",EDGE,"E110")])]})});
            var Q4;
            Q4=makeQuery(id+"F9.boolean.opBoolean","COPY",EDGE,{"derivedFrom":makeQuery(id+"F9.opExtrude","SWEPT_EDGE",EDGE,{"disambiguationData":[OSD([sQuery(id+"F8.wireOp",EDGE,"E90"),sQuery(id+"F8.wireOp",EDGE,"E113")])]})});
            var Q5;
            Q5=makeQuery(id+"F9.boolean.opBoolean","COPY",EDGE,{"derivedFrom":makeQuery(id+"F9.opExtrude","SWEPT_EDGE",EDGE,{"disambiguationData":[OSD([sQuery(id+"F8.wireOp",EDGE,"E103"),sQuery(id+"F8.wireOp",EDGE,"E114")])]})});
            var Q6;
            Q6=makeQuery(id+"F9.boolean.opBoolean","COPY",EDGE,{"derivedFrom":makeQuery(id+"F9.opExtrude","SWEPT_EDGE",EDGE,{"disambiguationData":[OSD([sQuery(id+"F8.wireOp",EDGE,"E106"),sQuery(id+"F8.wireOp",EDGE,"E115")])]})});
            var Q7;
            Q7=makeQuery(id+"F9.boolean.opBoolean","COPY",EDGE,{"derivedFrom":makeQuery(id+"F9.opExtrude","SWEPT_EDGE",EDGE,{"disambiguationData":[OSD([sQuery(id+"F8.wireOp",EDGE,"E100"),sQuery(id+"F8.wireOp",EDGE,"E116")])]})});
            var Q8;
            {var subQ0=sQuery(id+"F0.wireOp",EDGE,"E23");var subQ1=sQuery(id+"F0.wireOp",EDGE,"E22");Q8=makeQuery(id+"F9.boolean.opBoolean","MERGE",EDGE,{"derivedFrom":[makeQuery(id+"F1.opExtrude","SWEPT_EDGE",EDGE,{"disambiguationData":[OSD([subQ1,subQ0])]})],"fromTools":[makeQuery(id+"F9.opExtrude","SWEPT_EDGE",EDGE,{"disambiguationData":[OSD([subQ1,subQ0,sQuery(id+"F8.wireOp",EDGE,"E88"),sQuery(id+"F8.wireOp",EDGE,"E111")])]})]});}
            var Q9;
            {var subQ0=sQuery(id+"F0.wireOp",EDGE,"E24");var subQ1=sQuery(id+"F0.wireOp",EDGE,"E22");Q9=makeQuery(id+"F9.boolean.opBoolean","MERGE",EDGE,{"derivedFrom":[makeQuery(id+"F1.opExtrude","SWEPT_EDGE",EDGE,{"disambiguationData":[OSD([subQ1,subQ0])]})],"fromTools":[makeQuery(id+"F9.opExtrude","SWEPT_EDGE",EDGE,{"disambiguationData":[OSD([subQ1,subQ0,sQuery(id+"F8.wireOp",EDGE,"E87"),sQuery(id+"F8.wireOp",EDGE,"E110")])]})]});}
            var Q10;
            {var subQ0=sQuery(id+"F0.wireOp",EDGE,"E19");var subQ1=sQuery(id+"F0.wireOp",EDGE,"E18");Q10=makeQuery(id+"F9.boolean.opBoolean","MERGE",EDGE,{"derivedFrom":[makeQuery(id+"F1.opExtrude","SWEPT_EDGE",EDGE,{"disambiguationData":[OSD([subQ1,subQ0])]})],"fromTools":[makeQuery(id+"F9.opExtrude","SWEPT_EDGE",EDGE,{"disambiguationData":[OSD([subQ1,subQ0,sQuery(id+"F8.wireOp",EDGE,"E93"),sQuery(id+"F8.wireOp",EDGE,"E112")])]})]});}
            var Q11;
            {var subQ0=sQuery(id+"F0.wireOp",EDGE,"E20");var subQ1=sQuery(id+"F0.wireOp",EDGE,"E18");Q11=makeQuery(id+"F9.boolean.opBoolean","MERGE",EDGE,{"derivedFrom":[makeQuery(id+"F1.opExtrude","SWEPT_EDGE",EDGE,{"disambiguationData":[OSD([subQ1,subQ0])]})],"fromTools":[makeQuery(id+"F9.opExtrude","SWEPT_EDGE",EDGE,{"disambiguationData":[OSD([subQ1,subQ0,sQuery(id+"F8.wireOp",EDGE,"E95"),sQuery(id+"F8.wireOp",EDGE,"E113")])]})]});}
            var Q12;
            {var subQ0=sQuery(id+"F0.wireOp",EDGE,"E37");var subQ1=sQuery(id+"F0.wireOp",EDGE,"E36");Q12=makeQuery(id+"F9.boolean.opBoolean","MERGE",EDGE,{"derivedFrom":[makeQuery(id+"F1.opExtrude","SWEPT_EDGE",EDGE,{"disambiguationData":[OSD([subQ1,subQ0])]})],"fromTools":[makeQuery(id+"F9.opExtrude","SWEPT_EDGE",EDGE,{"disambiguationData":[OSD([subQ1,subQ0,sQuery(id+"F8.wireOp",EDGE,"E97"),sQuery(id+"F8.wireOp",EDGE,"E117")])]})]});}
            var Q13;
            {var subQ0=sQuery(id+"F0.wireOp",EDGE,"E38");var subQ1=sQuery(id+"F0.wireOp",EDGE,"E36");Q13=makeQuery(id+"F9.boolean.opBoolean","MERGE",EDGE,{"derivedFrom":[makeQuery(id+"F1.opExtrude","SWEPT_EDGE",EDGE,{"disambiguationData":[OSD([subQ1,subQ0])]})],"fromTools":[makeQuery(id+"F9.opExtrude","SWEPT_EDGE",EDGE,{"disambiguationData":[OSD([subQ1,subQ0,sQuery(id+"F8.wireOp",EDGE,"E102"),sQuery(id+"F8.wireOp",EDGE,"E116")])]})]});}
            var Q14;
            {var subQ0=sQuery(id+"F0.wireOp",EDGE,"E42");var subQ1=sQuery(id+"F0.wireOp",EDGE,"E40");Q14=makeQuery(id+"F9.boolean.opBoolean","MERGE",EDGE,{"derivedFrom":[makeQuery(id+"F1.opExtrude","SWEPT_EDGE",EDGE,{"disambiguationData":[OSD([subQ1,subQ0])]})],"fromTools":[makeQuery(id+"F9.opExtrude","SWEPT_EDGE",EDGE,{"disambiguationData":[OSD([subQ1,subQ0,sQuery(id+"F8.wireOp",EDGE,"E109"),sQuery(id+"F8.wireOp",EDGE,"E115")])]})]});}
            var Q15;
            {var subQ0=sQuery(id+"F0.wireOp",EDGE,"E41");var subQ1=sQuery(id+"F0.wireOp",EDGE,"E40");Q15=makeQuery(id+"F9.boolean.opBoolean","MERGE",EDGE,{"derivedFrom":[makeQuery(id+"F1.opExtrude","SWEPT_EDGE",EDGE,{"disambiguationData":[OSD([subQ1,subQ0])]})],"fromTools":[makeQuery(id+"F9.opExtrude","SWEPT_EDGE",EDGE,{"disambiguationData":[OSD([subQ1,subQ0,sQuery(id+"F8.wireOp",EDGE,"E105"),sQuery(id+"F8.wireOp",EDGE,"E114")])]})]});}
            fillet(context, id + "F10", {"entities" : qUnion([Q0, Q1, Q2, Q3, Q4, Q5, Q6, Q7, Q8, Q9, Q10, Q11, Q12, Q13, Q14, Q15]), "radius" : 5 * mm, "tangentPropagation" : true, "allowEdgeOverflow" : false});
        }
        {
            var Q0;
            Q0=makeQuery(id+"F9.boolean.opBoolean","COPY",EDGE,{"derivedFrom":makeQuery(id+"F9.opExtrude","SWEPT_EDGE",EDGE,{"disambiguationData":[OSD([sQuery(id+"F8.wireOp",EDGE,"E82"),sQuery(id+"F8.wireOp",EDGE,"E84")])]})});
            var Q1;
            Q1=makeQuery(id+"F9.boolean.opBoolean","COPY",EDGE,{"derivedFrom":makeQuery(id+"F9.opExtrude","SWEPT_EDGE",EDGE,{"disambiguationData":[OSD([sQuery(id+"F8.wireOp",EDGE,"E89"),sQuery(id+"F8.wireOp",EDGE,"E91")])]})});
            var Q2;
            Q2=makeQuery(id+"F9.boolean.opBoolean","COPY",EDGE,{"derivedFrom":makeQuery(id+"F9.opExtrude","SWEPT_EDGE",EDGE,{"disambiguationData":[OSD([sQuery(id+"F8.wireOp",EDGE,"E98"),sQuery(id+"F8.wireOp",EDGE,"E99")])]})});
            var Q3;
            Q3=makeQuery(id+"F9.boolean.opBoolean","COPY",EDGE,{"derivedFrom":makeQuery(id+"F9.opExtrude","SWEPT_EDGE",EDGE,{"disambiguationData":[OSD([sQuery(id+"F8.wireOp",EDGE,"E106"),sQuery(id+"F8.wireOp",EDGE,"E107")])]})});
            fillet(context, id + "F11", {"entities" : qUnion([Q0, Q1, Q2, Q3]), "radius" : 1 * mm, "tangentPropagation" : true, "allowEdgeOverflow" : false});
        }
        {
            var Q0;
            Q0=makeQuery(id+"F9.boolean.opBoolean","COPY",EDGE,{"derivedFrom":makeQuery(id+"F9.opExtrude","SWEPT_EDGE",EDGE,{"disambiguationData":[OSD([sQuery(id+"F8.wireOp",EDGE,"E83"),sQuery(id+"F8.wireOp",EDGE,"MxGTGzPo-W6f3-438L-qafL-rOFwTBjQn0TW")])]})});
            var Q1;
            Q1=makeQuery(id+"F9.boolean.opBoolean","COPY",EDGE,{"derivedFrom":makeQuery(id+"F9.opExtrude","SWEPT_EDGE",EDGE,{"disambiguationData":[OSD([sQuery(id+"F8.wireOp",EDGE,"E90"),sQuery(id+"F8.wireOp",EDGE,"VgRoDLYT-JpfP-qNXR-Oskc-2MysTVomEv5Y")])]})});
            var Q2;
            Q2=makeQuery(id+"F9.boolean.opBoolean","COPY",EDGE,{"derivedFrom":makeQuery(id+"F9.opExtrude","SWEPT_EDGE",EDGE,{"disambiguationData":[OSD([sQuery(id+"F8.wireOp",EDGE,"E103"),sQuery(id+"F8.wireOp",EDGE,"az7e6JTF-fPQg-SsSH-uCcW-VukgTpoLcSjs")])]})});
            var Q3;
            Q3=makeQuery(id+"F9.boolean.opBoolean","COPY",EDGE,{"derivedFrom":makeQuery(id+"F9.opExtrude","SWEPT_EDGE",EDGE,{"disambiguationData":[OSD([sQuery(id+"F8.wireOp",EDGE,"E100"),sQuery(id+"F8.wireOp",EDGE,"BavjTIyY-Kg86-IHXu-H5Rf-egFVTirOZPym")])]})});
            fillet(context, id + "F12", {"entities" : qUnion([Q0, Q1, Q2, Q3]), "radius" : 10 * mm, "tangentPropagation" : true, "allowEdgeOverflow" : false});
        }
        {
            var Q0;
            Q0=makeQuery(id+"F3.boolean.opBoolean","MERGE",FACE,{"derivedFrom":[makeQuery(id+"F1.opExtrude","CAP_FACE",FACE,{"disambiguationData":[OSD([sQuery(id+"F0.wireOp",EDGE,"E1"),sQuery(id+"F0.wireOp",EDGE,"E2"),sQuery(id+"F0.wireOp",EDGE,"E3"),sQuery(id+"F0.wireOp",EDGE,"E4"),sQuery(id+"F0.wireOp",EDGE,"E5.left"),sQuery(id+"F0.wireOp",EDGE,"E5.right"),sQuery(id+"F0.wireOp",EDGE,"E6.top"),sQuery(id+"F0.wireOp",EDGE,"E6.left"),sQuery(id+"F0.wireOp",EDGE,"E6.right"),sQuery(id+"F0.wireOp",EDGE,"E7.bottom"),sQuery(id+"F0.wireOp",EDGE,"E7.top"),sQuery(id+"F0.wireOp",EDGE,"E7.left"),sQuery(id+"F0.wireOp",EDGE,"E7.right"),sQuery(id+"F0.wireOp",EDGE,"E8.bottom"),sQuery(id+"F0.wireOp",EDGE,"E8.top"),sQuery(id+"F0.wireOp",EDGE,"E8.left"),sQuery(id+"F0.wireOp",EDGE,"E8.right"),sQuery(id+"F0.wireOp",EDGE,"E9.top"),sQuery(id+"F0.wireOp",EDGE,"E9.left"),sQuery(id+"F0.wireOp",EDGE,"E9.right"),sQuery(id+"F0.wireOp",EDGE,"E15"),sQuery(id+"F0.wireOp",EDGE,"E16"),sQuery(id+"F0.wireOp",EDGE,"E18"),sQuery(id+"F0.wireOp",EDGE,"E19"),sQuery(id+"F0.wireOp",EDGE,"E20"),sQuery(id+"F0.wireOp",EDGE,"E22"),sQuery(id+"F0.wireOp",EDGE,"E23"),sQuery(id+"F0.wireOp",EDGE,"E24"),sQuery(id+"F0.wireOp",EDGE,"E26"),sQuery(id+"F0.wireOp",EDGE,"E27"),sQuery(id+"F0.wireOp",EDGE,"E28"),sQuery(id+"F0.wireOp",EDGE,"E29"),sQuery(id+"F0.wireOp",EDGE,"E30"),sQuery(id+"F0.wireOp",EDGE,"E36"),sQuery(id+"F0.wireOp",EDGE,"E37"),sQuery(id+"F0.wireOp",EDGE,"E38"),sQuery(id+"F0.wireOp",EDGE,"E40"),sQuery(id+"F0.wireOp",EDGE,"E41"),sQuery(id+"F0.wireOp",EDGE,"E42"),sQuery(id+"F0.wireOp",EDGE,"E44"),sQuery(id+"F0.wireOp",EDGE,"E45"),sQuery(id+"F0.wireOp",EDGE,"E46"),sQuery(id+"F0.wireOp",EDGE,"E47"),sQuery(id+"F0.wireOp",EDGE,"E48"),sQuery(id+"F0.wireOp",EDGE,"E50"),sQuery(id+"F0.wireOp",EDGE,"E51"),sQuery(id+"F0.wireOp",EDGE,"E52"),sQuery(id+"F0.wireOp",EDGE,"E53"),sQuery(id+"F0.wireOp",EDGE,"E54"),sQuery(id+"F0.wireOp",EDGE,"E56"),sQuery(id+"F0.wireOp",EDGE,"E57"),sQuery(id+"F0.wireOp",EDGE,"E58"),sQuery(id+"F0.wireOp",EDGE,"E59"),sQuery(id+"F0.wireOp",EDGE,"E60"),sQuery(id+"F0.wireOp",EDGE,"E62")])],"isStart":false}),makeQuery(id+"F3.opExtrude","CAP_FACE",FACE,{"disambiguationData":[OSD([sQuery(id+"F2.wireOp",EDGE,"E71"),sQuery(id+"F2.wireOp",EDGE,"E72"),sQuery(id+"F2.wireOp",EDGE,"E73"),sQuery(id+"F2.wireOp",EDGE,"E74"),sQuery(id+"F2.wireOp",EDGE,"E75")])],"isStart":true})]});
            var sketch = newSketch(context, id + "F13", { "sketchPlane" : qUnion([Q0])});
            skPoint(sketch, "E120.endSnap0", {"position": v(-35.56, 36.29) * mm});
            skLineSegment(sketch, "E121", {"start": v(-43.43, 29.53) * mm, "end": v(-34.57, 31.09) * mm, "construction": true});
            skLineSegment(sketch, "E122", {"start": v(-34.57, 31.09) * mm, "end": v(-38.22, 25.88) * mm, "construction": true});
            skLineSegment(sketch, "E123", {"start": v(-38.22, 25.88) * mm, "end": v(-39.78, 34.74) * mm, "construction": true});
            skLineSegment(sketch, "E124", {"start": v(-39.78, 34.74) * mm, "end": v(-40.82, 40.65) * mm, "construction": true});
            skLineSegment(sketch, "E125", {"start": v(-43.43, 29.53) * mm, "end": v(-49.34, 28.48) * mm, "construction": true});
            skLineSegment(sketch, "E126", {"start": v(-41.7, 24.3) * mm, "end": v(-45.18, 25.03) * mm});
            skLineSegment(sketch, "E127", {"start": v(-45.18, 25.03) * mm, "end": v(-46.4, 31.95) * mm});
            skLineSegment(sketch, "E128", {"start": v(-34.27, 34.9) * mm, "end": v(-36.16, 37.92) * mm});
            skLineSegment(sketch, "E129", {"start": v(-36.16, 37.92) * mm, "end": v(-43.07, 36.7) * mm});
            skLineSegment(sketch, "E130", {"start": v(-43.07, 36.7) * mm, "end": v(-46.4, 31.95) * mm});
            skArc(sketch, "E131", {"start": v(-34.27, 34.9) * mm, "mid": v(-44.4, 34.09) * mm, "end": v(-41.7, 24.3) * mm});
            skLineSegment(sketch, "E132", {"start": v(39.78, 34.74) * mm, "end": v(38.22, 25.88) * mm, "construction": true});
            skLineSegment(sketch, "E133", {"start": v(38.22, 25.88) * mm, "end": v(34.57, 31.09) * mm, "construction": true});
            skLineSegment(sketch, "E134", {"start": v(34.57, 31.09) * mm, "end": v(43.43, 29.53) * mm, "construction": true});
            skLineSegment(sketch, "E135", {"start": v(43.43, 29.53) * mm, "end": v(49.34, 28.48) * mm, "construction": true});
            skLineSegment(sketch, "E136", {"start": v(39.78, 34.74) * mm, "end": v(40.82, 40.65) * mm, "construction": true});
            skLineSegment(sketch, "E137", {"start": v(34.27, 34.9) * mm, "end": v(36.16, 37.92) * mm});
            skLineSegment(sketch, "E138", {"start": v(36.16, 37.92) * mm, "end": v(43.07, 36.7) * mm});
            skLineSegment(sketch, "E139", {"start": v(43.07, 36.7) * mm, "end": v(46.4, 31.95) * mm});
            skLineSegment(sketch, "E140", {"start": v(46.4, 31.95) * mm, "end": v(45.18, 25.03) * mm});
            skLineSegment(sketch, "E141", {"start": v(45.18, 25.03) * mm, "end": v(41.7, 24.3) * mm});
            skArc(sketch, "E142", {"start": v(34.27, 34.9) * mm, "mid": v(44.4, 34.09) * mm, "end": v(41.7, 24.3) * mm});
            skLineSegment(sketch, "E143", {"start": v(-40.82, -40.65) * mm, "end": v(-39.78, -34.74) * mm, "construction": true});
            skLineSegment(sketch, "E144", {"start": v(-39.78, -34.74) * mm, "end": v(-38.22, -25.88) * mm, "construction": true});
            skLineSegment(sketch, "E145", {"start": v(-38.22, -25.88) * mm, "end": v(-34.57, -31.09) * mm, "construction": true});
            skLineSegment(sketch, "E146", {"start": v(-34.57, -31.09) * mm, "end": v(-43.43, -29.53) * mm, "construction": true});
            skLineSegment(sketch, "E147", {"start": v(-43.43, -29.53) * mm, "end": v(-49.34, -28.48) * mm, "construction": true});
            skLineSegment(sketch, "E148", {"start": v(-34.27, -34.9) * mm, "end": v(-36.16, -37.92) * mm});
            skLineSegment(sketch, "E149", {"start": v(-36.16, -37.92) * mm, "end": v(-43.07, -36.7) * mm});
            skLineSegment(sketch, "E150", {"start": v(-43.07, -36.7) * mm, "end": v(-46.4, -31.95) * mm});
            skLineSegment(sketch, "E151", {"start": v(-46.4, -31.95) * mm, "end": v(-45.18, -25.03) * mm});
            skLineSegment(sketch, "E152", {"start": v(-45.18, -25.03) * mm, "end": v(-41.7, -24.3) * mm});
            skArc(sketch, "E153", {"start": v(-41.7, -24.3) * mm, "mid": v(-44.4, -34.09) * mm, "end": v(-34.27, -34.9) * mm});
            skLineSegment(sketch, "E154", {"start": v(40.82, -40.65) * mm, "end": v(39.78, -34.74) * mm, "construction": true});
            skLineSegment(sketch, "E155", {"start": v(39.78, -34.74) * mm, "end": v(38.22, -25.88) * mm, "construction": true});
            skLineSegment(sketch, "E156", {"start": v(38.22, -25.88) * mm, "end": v(34.57, -31.09) * mm, "construction": true});
            skLineSegment(sketch, "E157", {"start": v(34.57, -31.09) * mm, "end": v(43.43, -29.53) * mm, "construction": true});
            skLineSegment(sketch, "E158", {"start": v(43.43, -29.53) * mm, "end": v(49.34, -28.48) * mm, "construction": true});
            skLineSegment(sketch, "E159", {"start": v(34.27, -34.9) * mm, "end": v(36.16, -37.92) * mm});
            skLineSegment(sketch, "E160", {"start": v(36.16, -37.92) * mm, "end": v(43.07, -36.7) * mm});
            skLineSegment(sketch, "E161", {"start": v(43.07, -36.7) * mm, "end": v(46.4, -31.95) * mm});
            skLineSegment(sketch, "E162", {"start": v(46.4, -31.95) * mm, "end": v(45.18, -25.03) * mm});
            skLineSegment(sketch, "E163", {"start": v(45.18, -25.03) * mm, "end": v(41.7, -24.3) * mm});
            skArc(sketch, "E164", {"start": v(41.7, -24.3) * mm, "mid": v(44.4, -34.09) * mm, "end": v(34.27, -34.9) * mm});
            skSolve(sketch);
        }
        {
            var Q0;
            Q0 = qSketchRegion(id + "F13", true);
            var Q1;
            Q1=makeQuery(id+"F3.boolean.opBoolean","MERGE",FACE,{"derivedFrom":[makeQuery(id+"F1.opExtrude","CAP_FACE",FACE,{"disambiguationData":[OSD([sQuery(id+"F0.wireOp",EDGE,"E1"),sQuery(id+"F0.wireOp",EDGE,"E2"),sQuery(id+"F0.wireOp",EDGE,"E3"),sQuery(id+"F0.wireOp",EDGE,"E4"),sQuery(id+"F0.wireOp",EDGE,"E5.left"),sQuery(id+"F0.wireOp",EDGE,"E5.right"),sQuery(id+"F0.wireOp",EDGE,"E6.top"),sQuery(id+"F0.wireOp",EDGE,"E6.left"),sQuery(id+"F0.wireOp",EDGE,"E6.right"),sQuery(id+"F0.wireOp",EDGE,"E7.bottom"),sQuery(id+"F0.wireOp",EDGE,"E7.top"),sQuery(id+"F0.wireOp",EDGE,"E7.left"),sQuery(id+"F0.wireOp",EDGE,"E7.right"),sQuery(id+"F0.wireOp",EDGE,"E8.bottom"),sQuery(id+"F0.wireOp",EDGE,"E8.top"),sQuery(id+"F0.wireOp",EDGE,"E8.left"),sQuery(id+"F0.wireOp",EDGE,"E8.right"),sQuery(id+"F0.wireOp",EDGE,"E9.top"),sQuery(id+"F0.wireOp",EDGE,"E9.left"),sQuery(id+"F0.wireOp",EDGE,"E9.right"),sQuery(id+"F0.wireOp",EDGE,"E15"),sQuery(id+"F0.wireOp",EDGE,"E16"),sQuery(id+"F0.wireOp",EDGE,"E18"),sQuery(id+"F0.wireOp",EDGE,"E19"),sQuery(id+"F0.wireOp",EDGE,"E20"),sQuery(id+"F0.wireOp",EDGE,"E22"),sQuery(id+"F0.wireOp",EDGE,"E23"),sQuery(id+"F0.wireOp",EDGE,"E24"),sQuery(id+"F0.wireOp",EDGE,"E26"),sQuery(id+"F0.wireOp",EDGE,"E27"),sQuery(id+"F0.wireOp",EDGE,"E28"),sQuery(id+"F0.wireOp",EDGE,"E29"),sQuery(id+"F0.wireOp",EDGE,"E30"),sQuery(id+"F0.wireOp",EDGE,"E36"),sQuery(id+"F0.wireOp",EDGE,"E37"),sQuery(id+"F0.wireOp",EDGE,"E38"),sQuery(id+"F0.wireOp",EDGE,"E40"),sQuery(id+"F0.wireOp",EDGE,"E41"),sQuery(id+"F0.wireOp",EDGE,"E42"),sQuery(id+"F0.wireOp",EDGE,"E44"),sQuery(id+"F0.wireOp",EDGE,"E45"),sQuery(id+"F0.wireOp",EDGE,"E46"),sQuery(id+"F0.wireOp",EDGE,"E47"),sQuery(id+"F0.wireOp",EDGE,"E48"),sQuery(id+"F0.wireOp",EDGE,"E50"),sQuery(id+"F0.wireOp",EDGE,"E51"),sQuery(id+"F0.wireOp",EDGE,"E52"),sQuery(id+"F0.wireOp",EDGE,"E53"),sQuery(id+"F0.wireOp",EDGE,"E54"),sQuery(id+"F0.wireOp",EDGE,"E56"),sQuery(id+"F0.wireOp",EDGE,"E57"),sQuery(id+"F0.wireOp",EDGE,"E58"),sQuery(id+"F0.wireOp",EDGE,"E59"),sQuery(id+"F0.wireOp",EDGE,"E60"),sQuery(id+"F0.wireOp",EDGE,"E62")])],"isStart":true}),makeQuery(id+"F3.opExtrude","CAP_FACE",FACE,{"disambiguationData":[OSD([sQuery(id+"F2.wireOp",EDGE,"E71"),sQuery(id+"F2.wireOp",EDGE,"E72"),sQuery(id+"F2.wireOp",EDGE,"E73"),sQuery(id+"F2.wireOp",EDGE,"E74"),sQuery(id+"F2.wireOp",EDGE,"E75")])],"isStart":false})]});
            extrude(context, id + "F14", {"entities" : qUnion([Q0]), "operationType" : NewBodyOperationType.ADD, "endBound" : BoundingType.UP_TO_SURFACE, "oppositeDirection" : true, "depth" : 25 * mm, "endBoundEntityFace" : qUnion([Q1]), "offsetDistance" : 25 * mm});
        }
        {
            var Q0;
            Q0=makeQuery(id+"F3.boolean.opBoolean","MERGE",FACE,{"derivedFrom":[makeQuery(id+"F1.opExtrude","CAP_FACE",FACE,{"disambiguationData":[OSD([sQuery(id+"F0.wireOp",EDGE,"E1"),sQuery(id+"F0.wireOp",EDGE,"E2"),sQuery(id+"F0.wireOp",EDGE,"E3"),sQuery(id+"F0.wireOp",EDGE,"E4"),sQuery(id+"F0.wireOp",EDGE,"E5.left"),sQuery(id+"F0.wireOp",EDGE,"E5.right"),sQuery(id+"F0.wireOp",EDGE,"E6.top"),sQuery(id+"F0.wireOp",EDGE,"E6.left"),sQuery(id+"F0.wireOp",EDGE,"E6.right"),sQuery(id+"F0.wireOp",EDGE,"E7.bottom"),sQuery(id+"F0.wireOp",EDGE,"E7.top"),sQuery(id+"F0.wireOp",EDGE,"E7.left"),sQuery(id+"F0.wireOp",EDGE,"E7.right"),sQuery(id+"F0.wireOp",EDGE,"E8.bottom"),sQuery(id+"F0.wireOp",EDGE,"E8.top"),sQuery(id+"F0.wireOp",EDGE,"E8.left"),sQuery(id+"F0.wireOp",EDGE,"E8.right"),sQuery(id+"F0.wireOp",EDGE,"E9.top"),sQuery(id+"F0.wireOp",EDGE,"E9.left"),sQuery(id+"F0.wireOp",EDGE,"E9.right"),sQuery(id+"F0.wireOp",EDGE,"E15"),sQuery(id+"F0.wireOp",EDGE,"E16"),sQuery(id+"F0.wireOp",EDGE,"E18"),sQuery(id+"F0.wireOp",EDGE,"E19"),sQuery(id+"F0.wireOp",EDGE,"E20"),sQuery(id+"F0.wireOp",EDGE,"E22"),sQuery(id+"F0.wireOp",EDGE,"E23"),sQuery(id+"F0.wireOp",EDGE,"E24"),sQuery(id+"F0.wireOp",EDGE,"E26"),sQuery(id+"F0.wireOp",EDGE,"E27"),sQuery(id+"F0.wireOp",EDGE,"E28"),sQuery(id+"F0.wireOp",EDGE,"E29"),sQuery(id+"F0.wireOp",EDGE,"E30"),sQuery(id+"F0.wireOp",EDGE,"E36"),sQuery(id+"F0.wireOp",EDGE,"E37"),sQuery(id+"F0.wireOp",EDGE,"E38"),sQuery(id+"F0.wireOp",EDGE,"E40"),sQuery(id+"F0.wireOp",EDGE,"E41"),sQuery(id+"F0.wireOp",EDGE,"E42"),sQuery(id+"F0.wireOp",EDGE,"E44"),sQuery(id+"F0.wireOp",EDGE,"E45"),sQuery(id+"F0.wireOp",EDGE,"E46"),sQuery(id+"F0.wireOp",EDGE,"E47"),sQuery(id+"F0.wireOp",EDGE,"E48"),sQuery(id+"F0.wireOp",EDGE,"E50"),sQuery(id+"F0.wireOp",EDGE,"E51"),sQuery(id+"F0.wireOp",EDGE,"E52"),sQuery(id+"F0.wireOp",EDGE,"E53"),sQuery(id+"F0.wireOp",EDGE,"E54"),sQuery(id+"F0.wireOp",EDGE,"E56"),sQuery(id+"F0.wireOp",EDGE,"E57"),sQuery(id+"F0.wireOp",EDGE,"E58"),sQuery(id+"F0.wireOp",EDGE,"E59"),sQuery(id+"F0.wireOp",EDGE,"E60")])],"isStart":false}),makeQuery(id+"F3.opExtrude","CAP_FACE",FACE,{"disambiguationData":[OSD([sQuery(id+"F2.wireOp",EDGE,"E71"),sQuery(id+"F2.wireOp",EDGE,"E72"),sQuery(id+"F2.wireOp",EDGE,"E73"),sQuery(id+"F2.wireOp",EDGE,"E74"),sQuery(id+"F2.wireOp",EDGE,"E75")])],"isStart":true})]});
            var sketch = newSketch(context, id + "F15", { "sketchPlane" : qUnion([Q0])});
            skLineSegment(sketch, "E165.bottom", {"start": v(4, 8) * mm, "end": v(-4, 8) * mm});
            skLineSegment(sketch, "E165.top", {"start": v(4, -8) * mm, "end": v(-4, -8) * mm});
            skLineSegment(sketch, "E165.left", {"start": v(7, 5) * mm, "end": v(7, -5) * mm});
            skLineSegment(sketch, "E165.right", {"start": v(-7, 5) * mm, "end": v(-7, -5) * mm});
            skPoint(sketch, "E165.middle", {"position": v(0, 0) * mm});
            skPoint(sketch, "E166.visualSharp", {"position": v(-7, 8) * mm});
            skArc(sketch, "E166.filletArc", {"start": v(-4, 8) * mm, "mid": v(-6.12, 7.12) * mm, "end": v(-7, 5) * mm});
            skPoint(sketch, "E167.visualSharp", {"position": v(7, 8) * mm});
            skArc(sketch, "E167.filletArc", {"start": v(7, 5) * mm, "mid": v(6.12, 7.12) * mm, "end": v(4, 8) * mm});
            skPoint(sketch, "E168.visualSharp", {"position": v(7, -8) * mm});
            skArc(sketch, "E168.filletArc", {"start": v(4, -8) * mm, "mid": v(6.12, -7.12) * mm, "end": v(7, -5) * mm});
            skPoint(sketch, "E169.visualSharp", {"position": v(-7, -8) * mm});
            skArc(sketch, "E169.filletArc", {"start": v(-7, -5) * mm, "mid": v(-6.12, -7.12) * mm, "end": v(-4, -8) * mm});
            skSolve(sketch);
        }
        {
            var Q0;
            Q0 = qSketchRegion(id + "F15", true);
            extrude(context, id + "F16", {"entities" : qUnion([Q0]), "operationType" : NewBodyOperationType.REMOVE, "endBound" : BoundingType.THROUGH_ALL, "oppositeDirection" : true, "depth" : 25 * mm, "offsetDistance" : 25 * mm});
        }
        {
            var Q0;
            Q0=makeQuery(id+"F3.boolean.opBoolean","MERGE",FACE,{"derivedFrom":[makeQuery(id+"F1.opExtrude","CAP_FACE",FACE,{"disambiguationData":[OSD([sQuery(id+"F0.wireOp",EDGE,"E1"),sQuery(id+"F0.wireOp",EDGE,"E2"),sQuery(id+"F0.wireOp",EDGE,"E3"),sQuery(id+"F0.wireOp",EDGE,"E4"),sQuery(id+"F0.wireOp",EDGE,"E5.left"),sQuery(id+"F0.wireOp",EDGE,"E5.right"),sQuery(id+"F0.wireOp",EDGE,"E6.top"),sQuery(id+"F0.wireOp",EDGE,"E6.left"),sQuery(id+"F0.wireOp",EDGE,"E6.right"),sQuery(id+"F0.wireOp",EDGE,"E7.bottom"),sQuery(id+"F0.wireOp",EDGE,"E7.top"),sQuery(id+"F0.wireOp",EDGE,"E7.left"),sQuery(id+"F0.wireOp",EDGE,"E7.right"),sQuery(id+"F0.wireOp",EDGE,"E8.bottom"),sQuery(id+"F0.wireOp",EDGE,"E8.top"),sQuery(id+"F0.wireOp",EDGE,"E8.left"),sQuery(id+"F0.wireOp",EDGE,"E8.right"),sQuery(id+"F0.wireOp",EDGE,"E9.top"),sQuery(id+"F0.wireOp",EDGE,"E9.left"),sQuery(id+"F0.wireOp",EDGE,"E9.right"),sQuery(id+"F0.wireOp",EDGE,"E15"),sQuery(id+"F0.wireOp",EDGE,"E16"),sQuery(id+"F0.wireOp",EDGE,"E18"),sQuery(id+"F0.wireOp",EDGE,"E19"),sQuery(id+"F0.wireOp",EDGE,"E20"),sQuery(id+"F0.wireOp",EDGE,"E22"),sQuery(id+"F0.wireOp",EDGE,"E23"),sQuery(id+"F0.wireOp",EDGE,"E24"),sQuery(id+"F0.wireOp",EDGE,"E26"),sQuery(id+"F0.wireOp",EDGE,"E27"),sQuery(id+"F0.wireOp",EDGE,"E28"),sQuery(id+"F0.wireOp",EDGE,"E29"),sQuery(id+"F0.wireOp",EDGE,"E30"),sQuery(id+"F0.wireOp",EDGE,"E36"),sQuery(id+"F0.wireOp",EDGE,"E37"),sQuery(id+"F0.wireOp",EDGE,"E38"),sQuery(id+"F0.wireOp",EDGE,"E40"),sQuery(id+"F0.wireOp",EDGE,"E41"),sQuery(id+"F0.wireOp",EDGE,"E42"),sQuery(id+"F0.wireOp",EDGE,"E44"),sQuery(id+"F0.wireOp",EDGE,"E45"),sQuery(id+"F0.wireOp",EDGE,"E46"),sQuery(id+"F0.wireOp",EDGE,"E47"),sQuery(id+"F0.wireOp",EDGE,"E48"),sQuery(id+"F0.wireOp",EDGE,"E50"),sQuery(id+"F0.wireOp",EDGE,"E51"),sQuery(id+"F0.wireOp",EDGE,"E52"),sQuery(id+"F0.wireOp",EDGE,"E53"),sQuery(id+"F0.wireOp",EDGE,"E54"),sQuery(id+"F0.wireOp",EDGE,"E56"),sQuery(id+"F0.wireOp",EDGE,"E57"),sQuery(id+"F0.wireOp",EDGE,"E58"),sQuery(id+"F0.wireOp",EDGE,"E59"),sQuery(id+"F0.wireOp",EDGE,"E60")])],"isStart":false}),makeQuery(id+"F3.opExtrude","CAP_FACE",FACE,{"disambiguationData":[OSD([sQuery(id+"F2.wireOp",EDGE,"E71"),sQuery(id+"F2.wireOp",EDGE,"E72"),sQuery(id+"F2.wireOp",EDGE,"E73"),sQuery(id+"F2.wireOp",EDGE,"E74"),sQuery(id+"F2.wireOp",EDGE,"E75")])],"isStart":true})]});
            var sketch = newSketch(context, id + "F17", { "sketchPlane" : qUnion([Q0])});
            skLineSegment(sketch, "E170", {"start": v(14.57, -18.09) * mm, "end": v(14.57, -34.02) * mm});
            skLineSegment(sketch, "E171", {"start": v(14.57, -34.02) * mm, "end": v(-14.57, -34.02) * mm});
            skLineSegment(sketch, "E172", {"start": v(-14.57, -34.02) * mm, "end": v(-14.57, -18.09) * mm});
            skLineSegment(sketch, "E173", {"start": v(-14.57, -18.09) * mm, "end": v(-9.66, -14.65) * mm});
            skLineSegment(sketch, "E174", {"start": v(-9.66, -14.65) * mm, "end": v(-9.66, -27.1) * mm});
            skLineSegment(sketch, "E175", {"start": v(0, -31) * mm, "end": v(-9.66, -27.1) * mm});
            skLineSegment(sketch, "E176", {"start": v(14.57, -18.09) * mm, "end": v(9.66, -14.65) * mm});
            skLineSegment(sketch, "E177", {"start": v(9.66, -14.65) * mm, "end": v(9.66, -27.1) * mm});
            skLineSegment(sketch, "E178", {"start": v(9.66, -27.1) * mm, "end": v(0, -31) * mm});
            skSolve(sketch);
        }
        {
            var Q0;
            Q0 = qSketchRegion(id + "F17", true);
            extrude(context, id + "F18", {"entities" : qUnion([Q0]), "operationType" : NewBodyOperationType.REMOVE, "endBound" : BoundingType.THROUGH_ALL, "oppositeDirection" : true, "depth" : 25 * mm, "offsetDistance" : 25 * mm});
        }
        {
            var Q0;
            Q0=makeQuery(id+"F18.boolean.opBoolean","COPY",EDGE,{"derivedFrom":makeQuery(id+"F18.opExtrude","SWEPT_EDGE",EDGE,{"disambiguationData":[OSD([sQuery(id+"F0.wireOp",EDGE,"E9.top"),sQuery(id+"F17.wireOp",EDGE,"E175"),sQuery(id+"F17.wireOp",EDGE,"E178")])]})});
            var Q1;
            Q1=makeQuery(id+"F18.boolean.opBoolean","COPY",EDGE,{"derivedFrom":makeQuery(id+"F18.opExtrude","SWEPT_EDGE",EDGE,{"disambiguationData":[OSD([sQuery(id+"F17.wireOp",EDGE,"E174"),sQuery(id+"F17.wireOp",EDGE,"E175")])]})});
            var Q2;
            Q2=makeQuery(id+"F18.boolean.opBoolean","COPY",EDGE,{"derivedFrom":makeQuery(id+"F18.opExtrude","SWEPT_EDGE",EDGE,{"disambiguationData":[OSD([sQuery(id+"F17.wireOp",EDGE,"E177"),sQuery(id+"F17.wireOp",EDGE,"E178")])]})});
            fillet(context, id + "F19", {"entities" : qUnion([Q0, Q1, Q2]), "radius" : 5 * mm, "tangentPropagation" : true, "allowEdgeOverflow" : false});
        }
        {
            var Q0;
            Q0=makeQuery(id+"F3.boolean.opBoolean","MERGE",FACE,{"derivedFrom":[makeQuery(id+"F1.opExtrude","CAP_FACE",FACE,{"disambiguationData":[OSD([sQuery(id+"F0.wireOp",EDGE,"E1"),sQuery(id+"F0.wireOp",EDGE,"E2"),sQuery(id+"F0.wireOp",EDGE,"E3"),sQuery(id+"F0.wireOp",EDGE,"E4"),sQuery(id+"F0.wireOp",EDGE,"E5.left"),sQuery(id+"F0.wireOp",EDGE,"E5.right"),sQuery(id+"F0.wireOp",EDGE,"E6.top"),sQuery(id+"F0.wireOp",EDGE,"E6.left"),sQuery(id+"F0.wireOp",EDGE,"E6.right"),sQuery(id+"F0.wireOp",EDGE,"E7.bottom"),sQuery(id+"F0.wireOp",EDGE,"E7.top"),sQuery(id+"F0.wireOp",EDGE,"E7.left"),sQuery(id+"F0.wireOp",EDGE,"E7.right"),sQuery(id+"F0.wireOp",EDGE,"E8.bottom"),sQuery(id+"F0.wireOp",EDGE,"E8.top"),sQuery(id+"F0.wireOp",EDGE,"E8.left"),sQuery(id+"F0.wireOp",EDGE,"E8.right"),sQuery(id+"F0.wireOp",EDGE,"E9.top"),sQuery(id+"F0.wireOp",EDGE,"E9.left"),sQuery(id+"F0.wireOp",EDGE,"E9.right"),sQuery(id+"F0.wireOp",EDGE,"E15"),sQuery(id+"F0.wireOp",EDGE,"E16"),sQuery(id+"F0.wireOp",EDGE,"E18"),sQuery(id+"F0.wireOp",EDGE,"E19"),sQuery(id+"F0.wireOp",EDGE,"E20"),sQuery(id+"F0.wireOp",EDGE,"E22"),sQuery(id+"F0.wireOp",EDGE,"E23"),sQuery(id+"F0.wireOp",EDGE,"E24"),sQuery(id+"F0.wireOp",EDGE,"E26"),sQuery(id+"F0.wireOp",EDGE,"E27"),sQuery(id+"F0.wireOp",EDGE,"E28"),sQuery(id+"F0.wireOp",EDGE,"E29"),sQuery(id+"F0.wireOp",EDGE,"E30"),sQuery(id+"F0.wireOp",EDGE,"E36"),sQuery(id+"F0.wireOp",EDGE,"E37"),sQuery(id+"F0.wireOp",EDGE,"E38"),sQuery(id+"F0.wireOp",EDGE,"E40"),sQuery(id+"F0.wireOp",EDGE,"E41"),sQuery(id+"F0.wireOp",EDGE,"E42"),sQuery(id+"F0.wireOp",EDGE,"E44"),sQuery(id+"F0.wireOp",EDGE,"E45"),sQuery(id+"F0.wireOp",EDGE,"E46"),sQuery(id+"F0.wireOp",EDGE,"E47"),sQuery(id+"F0.wireOp",EDGE,"E48"),sQuery(id+"F0.wireOp",EDGE,"E50"),sQuery(id+"F0.wireOp",EDGE,"E51"),sQuery(id+"F0.wireOp",EDGE,"E52"),sQuery(id+"F0.wireOp",EDGE,"E53"),sQuery(id+"F0.wireOp",EDGE,"E54"),sQuery(id+"F0.wireOp",EDGE,"E56"),sQuery(id+"F0.wireOp",EDGE,"E57"),sQuery(id+"F0.wireOp",EDGE,"E58"),sQuery(id+"F0.wireOp",EDGE,"E59"),sQuery(id+"F0.wireOp",EDGE,"E60"),sQuery(id+"F0.wireOp",EDGE,"E62")])],"isStart":false}),makeQuery(id+"F3.opExtrude","CAP_FACE",FACE,{"disambiguationData":[OSD([sQuery(id+"F2.wireOp",EDGE,"E71"),sQuery(id+"F2.wireOp",EDGE,"E72"),sQuery(id+"F2.wireOp",EDGE,"E73"),sQuery(id+"F2.wireOp",EDGE,"E74"),sQuery(id+"F2.wireOp",EDGE,"E75")])],"isStart":true})]});
            var sketch = newSketch(context, id + "F20", { "sketchPlane" : qUnion([Q0])});
            skLineSegment(sketch, "E179", {"start": v(-6.62, -13.96) * mm, "end": v(-6.55, -22.96) * mm});
            skPoint(sketch, "E179.startSnap0", {"position": v(-6.62, 27.98) * mm});
            skLineSegment(sketch, "E180", {"start": v(-6.55, -22.96) * mm, "end": v(0, -25.6) * mm});
            skLineSegment(sketch, "E181", {"start": v(0, -25.6) * mm, "end": v(7.07, -22.96) * mm});
            skLineSegment(sketch, "E182", {"start": v(7.07, -22.96) * mm, "end": v(7.07, -13.96) * mm});
            skLineSegment(sketch, "E183", {"start": v(7.07, -13.96) * mm, "end": v(-6.62, -13.96) * mm});
            skSolve(sketch);
        }
        {
            var Q0;
            Q0 = qSketchRegion(id + "F20", true);
            extrude(context, id + "F21", {"entities" : qUnion([Q0]), "operationType" : NewBodyOperationType.REMOVE, "endBound" : BoundingType.THROUGH_ALL, "oppositeDirection" : true, "depth" : 25 * mm, "offsetDistance" : 25 * mm});
        }
        {
            var Q0;
            Q0=makeQuery(id+"F21.boolean.opBoolean","COPY",EDGE,{"derivedFrom":makeQuery(id+"F21.opExtrude","SWEPT_EDGE",EDGE,{"disambiguationData":[OSD([sQuery(id+"F20.wireOp",EDGE,"E179"),sQuery(id+"F20.wireOp",EDGE,"E180")])]})});
            var Q1;
            Q1=makeQuery(id+"F21.boolean.opBoolean","COPY",EDGE,{"derivedFrom":makeQuery(id+"F21.opExtrude","SWEPT_EDGE",EDGE,{"disambiguationData":[OSD([sQuery(id+"F20.wireOp",EDGE,"E180"),sQuery(id+"F20.wireOp",EDGE,"E181")])]})});
            var Q2;
            Q2=makeQuery(id+"F21.boolean.opBoolean","COPY",EDGE,{"derivedFrom":makeQuery(id+"F21.opExtrude","SWEPT_EDGE",EDGE,{"disambiguationData":[OSD([sQuery(id+"F20.wireOp",EDGE,"E181"),sQuery(id+"F20.wireOp",EDGE,"E182")])]})});
            fillet(context, id + "F22", {"entities" : qUnion([Q0, Q1, Q2]), "radius" : 4 * mm, "tangentPropagation" : true, "allowEdgeOverflow" : false});
        }
        {
            var Q0;
            Q0=makeQuery(id+"F21.boolean.opBoolean","COPY",EDGE,{"derivedFrom":makeQuery(id+"F21.opExtrude","SWEPT_EDGE",EDGE,{"disambiguationData":[OSD([sQuery(id+"F20.wireOp",EDGE,"E179"),sQuery(id+"F20.wireOp",EDGE,"E183")])]})});
            var Q1;
            Q1=makeQuery(id+"F21.boolean.opBoolean","COPY",EDGE,{"derivedFrom":makeQuery(id+"F21.opExtrude","SWEPT_EDGE",EDGE,{"disambiguationData":[OSD([sQuery(id+"F20.wireOp",EDGE,"E182"),sQuery(id+"F20.wireOp",EDGE,"E183")])]})});
            fillet(context, id + "F23", {"entities" : qUnion([Q0, Q1]), "radius" : 1 * mm, "tangentPropagation" : true, "allowEdgeOverflow" : false});
        }
        {
            var Q0;
            Q0=makeQuery(id+"F18.boolean.opBoolean","COPY",EDGE,{"derivedFrom":makeQuery(id+"F18.opExtrude","SWEPT_EDGE",EDGE,{"disambiguationData":[OSD([sQuery(id+"F17.wireOp",EDGE,"E173"),sQuery(id+"F17.wireOp",EDGE,"E174")])]})});
            var Q1;
            Q1=makeQuery(id+"F18.boolean.opBoolean","COPY",EDGE,{"derivedFrom":makeQuery(id+"F18.opExtrude","SWEPT_EDGE",EDGE,{"disambiguationData":[OSD([sQuery(id+"F17.wireOp",EDGE,"E176"),sQuery(id+"F17.wireOp",EDGE,"E177")])]})});
            fillet(context, id + "F24", {"entities" : qUnion([Q0, Q1]), "radius" : 1 * mm, "tangentPropagation" : true, "allowEdgeOverflow" : false});
        }
    });
